# Revit family: Door_Swing Door_The Sliding Door Company_Single Door with Column & Beam_Without Casing
name_source: partatom
category: Doors
units: mm (PartAtom-declared; Revit-internal decimal feet)

## family parameters
Always vertical = Yes
Cut with Voids When Loaded = No
Host = Wall
OmniClass Number = 23.30.10.00
OmniClass Title = Doors
Room Calculation Point = No
Shared = No

## types (1)
- Single Swing Door with Column & Beam
    ADA Opening Clearance = Minimum of 32 inches Opening Clearance
    Beam = 2"
    Bottom Side Gap = 5/8"
    Column & Beam Sizes = Available Only in 2x4 & 4x4 Sizes
    Column at Handle Side = 2"
    Column at Hinge Side = 2"
    Description = Swing Door with Column & Beam
    Finished Opening Height = 90"
    Finished Opening Width = 40"
    Frame Projection Ext. = 1"
    Frame Projection Int. = 1"
    Frame Width = 3"
    Function = Interior
    Handle Side Gap = 1/8"
    Height = 90"
    Hinge Side Gap = 1/4"
    Manufacturer = The Sliding Door Company
    Maximum Door Panel Height = 108 inches
    Maximum Door Panel Width = 40 inches
    Maximum Door Swing = 120 degress
    Model = Swing Door with Column & Beam
    Opening Clearance Height = 89 1/2"
    Opening Clearance Width = 37 1/2"
    Overall System Height = 92"
    Overall System Width = 44"
    PULL = No
    PUSH = Yes
    Panel Height = 89 1/8"
    Panel Width = 39 5/8"
    Pull Kickplate = No
    Pull Lever Set = No
    Pull Round Designer Handle 12" = No
    Push Kickplate = Yes
    Push Lever Set = Yes
    Push Round Designer Handle 12" = No
    Stile/Rail = 3"
    Thickness = 1 1/4"
    Top Side Gap = 1/4"
    URL = https://www.slidingdoorco.com
    Wall Closure = By host
    Width = 40"

## geometry (parser evidence)
native form markers: Sweep x12
no freeform markers — native parametric forms only
